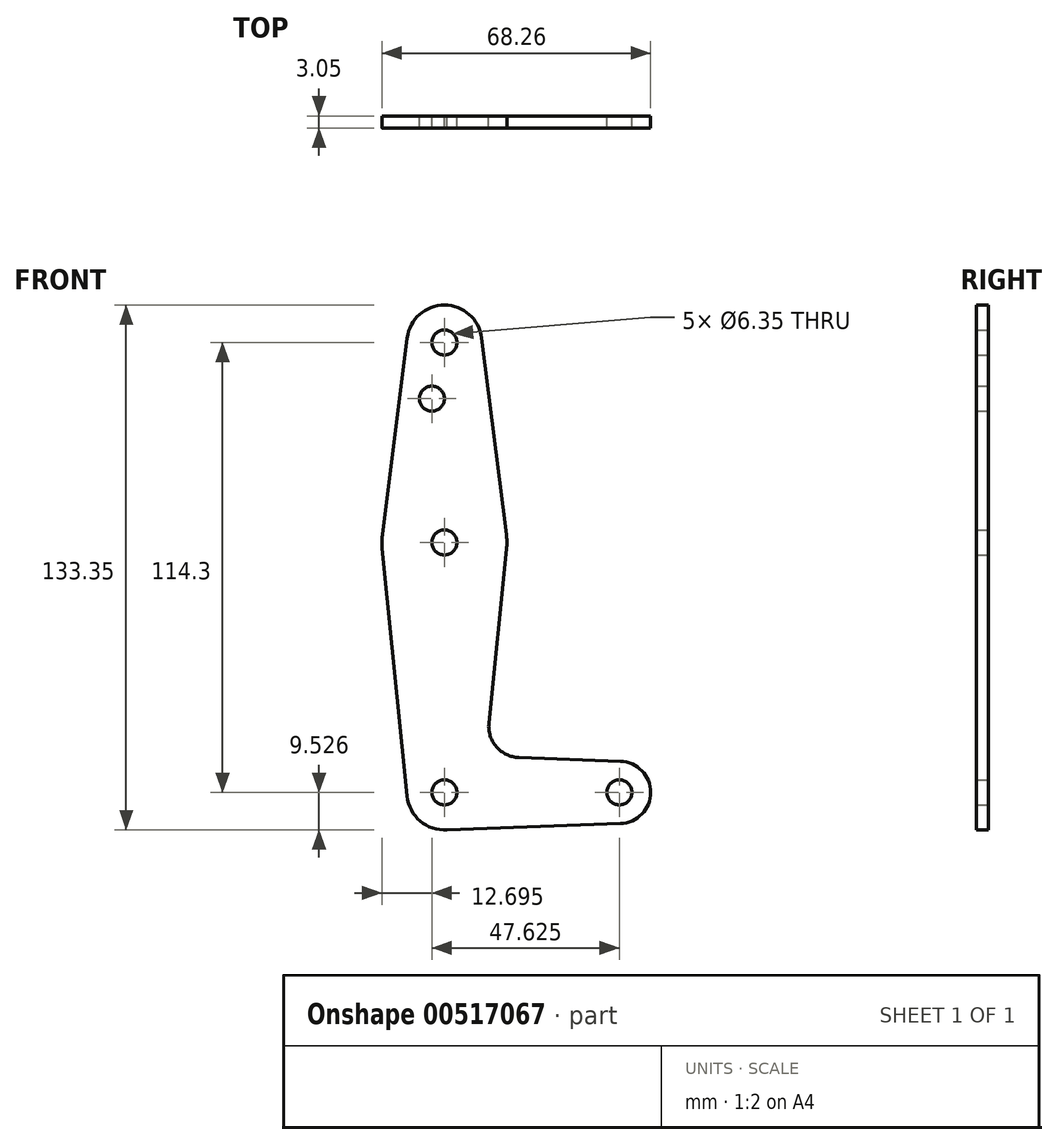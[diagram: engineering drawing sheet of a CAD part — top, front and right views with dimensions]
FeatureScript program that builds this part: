
annotation { "Feature Type Name" : "Feature", "Feature Type Description" : "" }
export const myFeature = defineFeature(function(context is Context, id is Id, definition is map)
    precondition{}
    {
        {
            var Q0;
            Q0=qCreatedBy(makeId("Front.planeOp"),FACE);
            var sketch = newSketch(context, id + "F0", { "sketchPlane" : qUnion([Q0])});
            skCircle(sketch, "E0", {"center": v(0, 34.62) * mm, "radius": 9.53 * mm});
            skCircle(sketch, "E1", {"center": v(0, -16.18) * mm, "radius": 15.88 * mm});
            skCircle(sketch, "E2", {"center": v(0, -79.68) * mm, "radius": 9.53 * mm});
            skCircle(sketch, "E3", {"center": v(44.45, -79.68) * mm, "radius": 7.94 * mm});
            skLineSegment(sketch, "E4", {"start": v(0, -16.18) * mm, "end": v(0, -79.68) * mm, "construction": true});
            skLineSegment(sketch, "E5", {"start": v(0, 34.62) * mm, "end": v(0, -16.18) * mm, "construction": true});
            skLineSegment(sketch, "E6", {"start": v(0, -79.68) * mm, "end": v(44.45, -79.68) * mm, "construction": true});
            skLineSegment(sketch, "E7", {"start": v(-15.8, -17.77) * mm, "end": v(-9.48, -80.64) * mm});
            skLineSegment(sketch, "E8", {"start": v(0, -89.2) * mm, "end": v(44.73, -87.62) * mm});
            skLineSegment(sketch, "E9", {"start": v(44.73, -71.75) * mm, "end": v(18.93, -70.83) * mm});
            skLineSegment(sketch, "E10", {"start": v(11.3, -62.08) * mm, "end": v(15.8, -17.78) * mm});
            skPoint(sketch, "E11.start.orphan", {"position": v(-9.52, 34.62) * mm});
            skLineSegment(sketch, "E12", {"start": v(-9.45, 35.8) * mm, "end": v(-15.75, -14.2) * mm});
            skLineSegment(sketch, "E13", {"start": v(15.75, -14.2) * mm, "end": v(9.45, 35.8) * mm});
            skCircle(sketch, "E14", {"center": v(0, 34.62) * mm, "radius": 3.18 * mm});
            skCircle(sketch, "E15", {"center": v(0, -16.18) * mm, "radius": 3.18 * mm});
            skCircle(sketch, "E16", {"center": v(0, -79.68) * mm, "radius": 3.18 * mm});
            skCircle(sketch, "E17", {"center": v(44.45, -79.68) * mm, "radius": 3.18 * mm});
            skCircle(sketch, "E18", {"center": v(-3.17, 20.34) * mm, "radius": 3.18 * mm});
            skArc(sketch, "E19.filletArc", {"start": v(11.3, -62.08) * mm, "mid": v(13.22, -68.1) * mm, "end": v(18.93, -70.83) * mm});
            skSolve(sketch);
        }
        {
            var Q0;
            Q0 = qSketchRegion(id + "F0", true);
            extrude(context, id + "F1", {"entities" : qUnion([Q0]), "depth" : 3.05 * mm, "offsetDistance" : 25.4 * mm});
        }
    });
